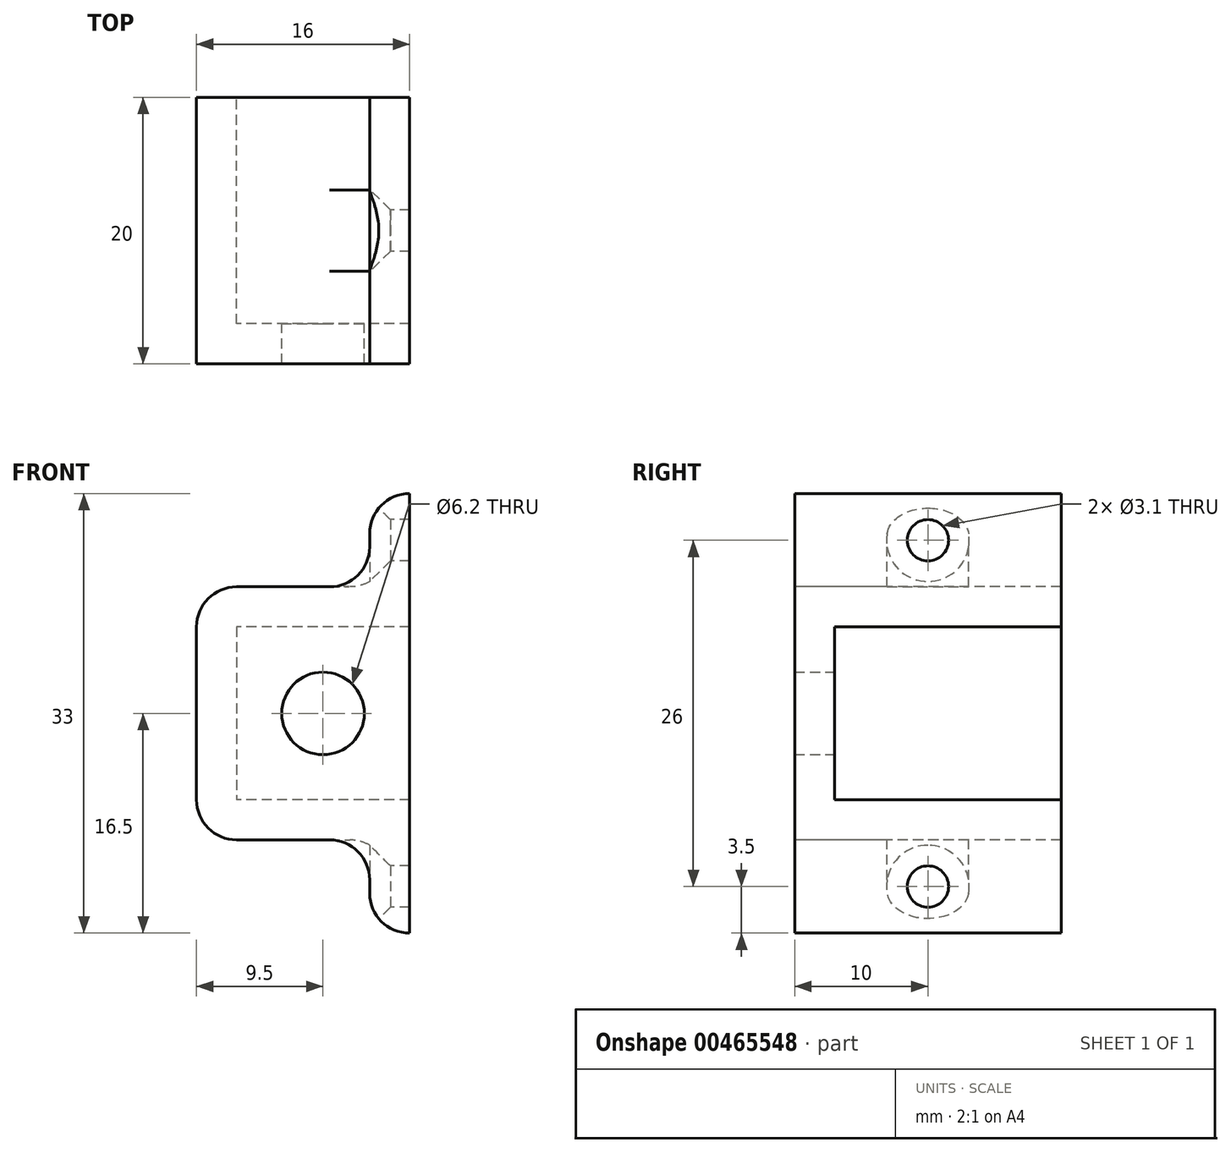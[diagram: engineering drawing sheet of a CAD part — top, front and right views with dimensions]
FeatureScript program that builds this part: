
annotation { "Feature Type Name" : "Feature", "Feature Type Description" : "" }
export const myFeature = defineFeature(function(context is Context, id is Id, definition is map)
    precondition{}
    {
        {
            var Q0;
            Q0=qCreatedBy(makeId("Front.planeOp"),FACE);
            var sketch = newSketch(context, id + "F0", { "sketchPlane" : qUnion([Q0])});
            skLineSegment(sketch, "E0", {"start": v(0, 19) * mm, "end": v(-13, 19) * mm});
            skLineSegment(sketch, "E1", {"start": v(-13, 19) * mm, "end": v(-13, 0) * mm});
            skLineSegment(sketch, "E2", {"start": v(-13, 0) * mm, "end": v(0, 0) * mm});
            skLineSegment(sketch, "E3", {"start": v(0, 0) * mm, "end": v(0, -7) * mm});
            skLineSegment(sketch, "E4", {"start": v(0, -7) * mm, "end": v(3, -7) * mm});
            skLineSegment(sketch, "E5", {"start": v(3, -7) * mm, "end": v(3, 26) * mm});
            skLineSegment(sketch, "E6", {"start": v(3, 26) * mm, "end": v(0, 26) * mm});
            skLineSegment(sketch, "E7", {"start": v(0, 26) * mm, "end": v(0, 19) * mm});
            skSolve(sketch);
        }
        {
            var Q0;
            Q0=makeQuery(id+"F0.imprint","IMPRINT",FACE,{"disambiguationData":[TD([[makeQuery(id+"F0.imprint","IMPRINT",EDGE,{"derivedFrom":sQuery(id+"F0.wireOp",EDGE,"E0")}),1.0]])]});
            extrude(context, id + "F1", {"entities" : qUnion([Q0]), "oppositeDirection" : true, "depth" : 20 * mm});
        }
        {
            var Q0;
            Q0=makeQuery(id+"F1.opExtrude","CAP_FACE",FACE,{"disambiguationData":[OSD([sQuery(id+"F0.wireOp",EDGE,"E0"),sQuery(id+"F0.wireOp",EDGE,"E1"),sQuery(id+"F0.wireOp",EDGE,"E2"),sQuery(id+"F0.wireOp",EDGE,"E3"),sQuery(id+"F0.wireOp",EDGE,"E4"),sQuery(id+"F0.wireOp",EDGE,"E5"),sQuery(id+"F0.wireOp",EDGE,"E6"),sQuery(id+"F0.wireOp",EDGE,"E7")])],"isStart":false});
            var sketch = newSketch(context, id + "F2", { "sketchPlane" : qUnion([Q0])});
            skLineSegment(sketch, "E8.bottom", {"start": v(-3, 16) * mm, "end": v(10, 16) * mm});
            skLineSegment(sketch, "E8.top", {"start": v(-3, 3) * mm, "end": v(10, 3) * mm});
            skLineSegment(sketch, "E8.left", {"start": v(-3, 16) * mm, "end": v(-3, 3) * mm});
            skLineSegment(sketch, "E8.right", {"start": v(10, 16) * mm, "end": v(10, 3) * mm});
            skSolve(sketch);
        }
        {
            var Q0;
            Q0=makeQuery(id+"F2.imprint","IMPRINT",FACE,{"disambiguationData":[TD([[makeQuery(id+"F2.imprint","IMPRINT",EDGE,{"derivedFrom":sQuery(id+"F2.wireOp",EDGE,"E8.bottom")}),-1.0]])]});
            extrude(context, id + "F3", {"entities" : qUnion([Q0]), "operationType" : NewBodyOperationType.REMOVE, "oppositeDirection" : true, "depth" : 17 * mm});
        }
        {
            var Q0;
            Q0=makeQuery(id+"F3.boolean.opBoolean","COPY",FACE,{"derivedFrom":makeQuery(id+"F3.opExtrude","CAP_FACE",FACE,{"disambiguationData":[OSD([sQuery(id+"F2.wireOp",EDGE,"E8.bottom"),sQuery(id+"F2.wireOp",EDGE,"E8.top"),sQuery(id+"F2.wireOp",EDGE,"E8.left"),sQuery(id+"F2.wireOp",EDGE,"E8.right")])],"isStart":false})});
            var sketch = newSketch(context, id + "F4", { "sketchPlane" : qUnion([Q0])});
            skPoint(sketch, "E9", {"position": v(3.5, 9.5) * mm});
            skSolve(sketch);
        }
        {
            var Q0;
            Q0=sQuery(id+"F4.wireOp",VERTEX,"E9");
            var Q1;
            Q1=makeQuery(id+"F1.opExtrude","SWEPT_BODY",BODY,{"disambiguationData":[OSD([sQuery(id+"F0.wireOp",EDGE,"E0"),sQuery(id+"F0.wireOp",EDGE,"E1"),sQuery(id+"F0.wireOp",EDGE,"E2"),sQuery(id+"F0.wireOp",EDGE,"E3"),sQuery(id+"F0.wireOp",EDGE,"E4"),sQuery(id+"F0.wireOp",EDGE,"E5"),sQuery(id+"F0.wireOp",EDGE,"E6"),sQuery(id+"F0.wireOp",EDGE,"E7")])]});
            hole(context, id + "F5", {"style" : HoleStyle.SIMPLE, "endStyle" : HoleEndStyle.THROUGH, "holeDiameter" : 6.2 * mm, "tappedDepth" : 12 * mm, "tapClearance" : 3, "locations" : qUnion([Q0]), "scope" : qUnion([Q1])});
        }
        {
            var Q0;
            Q0=makeQuery(id+"F1.opExtrude","SWEPT_FACE",FACE,{"disambiguationData":[OSD([sQuery(id+"F0.wireOp",EDGE,"E7")])]});
            var sketch = newSketch(context, id + "F6", { "sketchPlane" : qUnion([Q0])});
            skPoint(sketch, "E10", {"position": v(-10, 22.5) * mm});
            skPoint(sketch, "E11", {"position": v(-10, -3.5) * mm});
            skSolve(sketch);
        }
        {
            var Q0;
            Q0=sQuery(id+"F6.wireOp",VERTEX,"E10");
            var Q1;
            Q1=sQuery(id+"F6.wireOp",VERTEX,"E11");
            var Q2;
            Q2=makeQuery(id+"F1.opExtrude","SWEPT_BODY",BODY,{"disambiguationData":[OSD([sQuery(id+"F0.wireOp",EDGE,"E0"),sQuery(id+"F0.wireOp",EDGE,"E1"),sQuery(id+"F0.wireOp",EDGE,"E2"),sQuery(id+"F0.wireOp",EDGE,"E3"),sQuery(id+"F0.wireOp",EDGE,"E4"),sQuery(id+"F0.wireOp",EDGE,"E5"),sQuery(id+"F0.wireOp",EDGE,"E6"),sQuery(id+"F0.wireOp",EDGE,"E7")])]});
            hole(context, id + "F7", {"style" : HoleStyle.C_SINK, "endStyle" : HoleEndStyle.THROUGH, "holeDiameter" : 3.1 * mm, "cSinkDiameter" : 6.2 * mm, "cSinkAngle" : 90 * degree, "tappedDepth" : 12 * mm, "tapClearance" : 3, "locations" : qUnion([Q0, Q1]), "scope" : qUnion([Q2])});
        }
        {
            var Q0;
            Q0=makeQuery(id+"F1.opExtrude","SWEPT_EDGE",EDGE,{"disambiguationData":[OSD([sQuery(id+"F0.wireOp",EDGE,"E0"),sQuery(id+"F0.wireOp",EDGE,"E1")])]});
            var Q1;
            Q1=makeQuery(id+"F1.opExtrude","SWEPT_EDGE",EDGE,{"disambiguationData":[OSD([sQuery(id+"F0.wireOp",EDGE,"E1"),sQuery(id+"F0.wireOp",EDGE,"E2")])]});
            var Q2;
            Q2=makeQuery(id+"F1.opExtrude","SWEPT_EDGE",EDGE,{"disambiguationData":[OSD([sQuery(id+"F0.wireOp",EDGE,"E3"),sQuery(id+"F0.wireOp",EDGE,"E4")])]});
            var Q3;
            Q3=makeQuery(id+"F1.opExtrude","SWEPT_EDGE",EDGE,{"disambiguationData":[OSD([sQuery(id+"F0.wireOp",EDGE,"E6"),sQuery(id+"F0.wireOp",EDGE,"E7")])]});
            var Q4;
            Q4=makeQuery(id+"F1.opExtrude","SWEPT_EDGE",EDGE,{"disambiguationData":[OSD([sQuery(id+"F0.wireOp",EDGE,"E0"),sQuery(id+"F0.wireOp",EDGE,"E7")])]});
            var Q5;
            Q5=makeQuery(id+"F1.opExtrude","SWEPT_EDGE",EDGE,{"disambiguationData":[OSD([sQuery(id+"F0.wireOp",EDGE,"E2"),sQuery(id+"F0.wireOp",EDGE,"E3")])]});
            fillet(context, id + "F8", {"entities" : qUnion([Q0, Q1, Q2, Q3, Q4, Q5]), "radius" : 3 * mm, "tangentPropagation" : true, "allowEdgeOverflow" : false});
        }
    });
